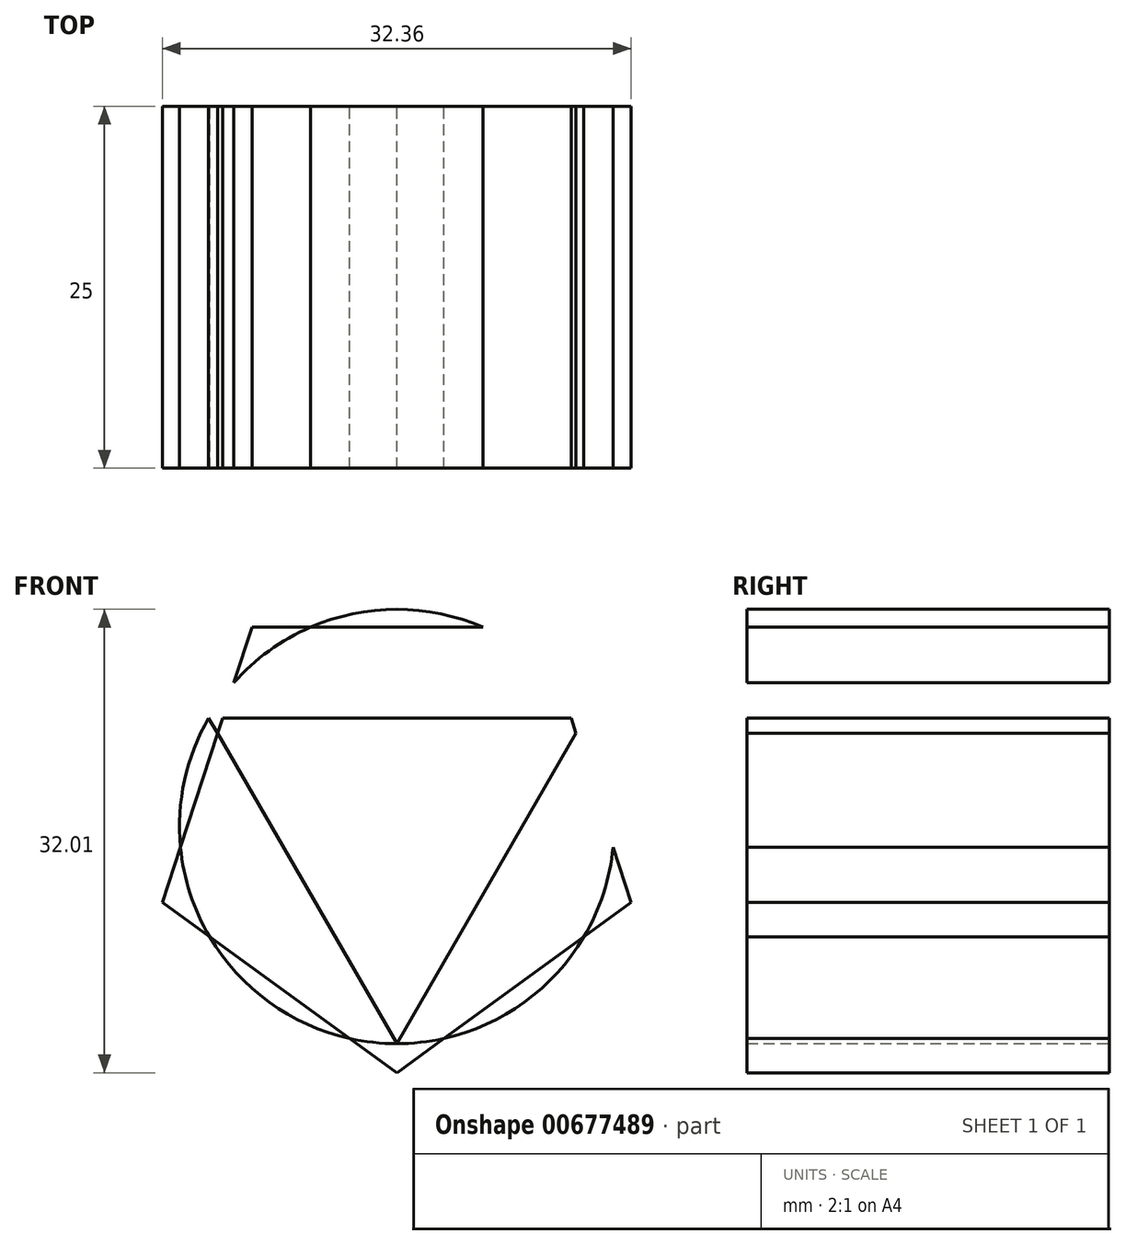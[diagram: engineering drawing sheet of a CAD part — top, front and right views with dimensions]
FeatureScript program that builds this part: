
annotation { "Feature Type Name" : "Feature", "Feature Type Description" : "" }
export const myFeature = defineFeature(function(context is Context, id is Id, definition is map)
    precondition{}
    {
        {
            var Q0;
            Q0=qCreatedBy(makeId("Front.planeOp"),FACE);
            var sketch = newSketch(context, id + "F0", { "sketchPlane" : qUnion([Q0])});
            skCircle(sketch, "E0", {"center": v(0, 0) * mm, "radius": 15 * mm});
            skCircle(sketch, "E1.cCircle", {"center": v(0, 0) * mm, "radius": 13.76 * mm, "construction": true});
            skLineSegment(sketch, "E1.0", {"start": v(10, 13.76) * mm, "end": v(-10, 13.76) * mm});
            skLineSegment(sketch, "E1.1", {"start": v(16.18, -5.26) * mm, "end": v(10, 13.76) * mm});
            skLineSegment(sketch, "E1.2", {"start": v(0, -17.01) * mm, "end": v(16.18, -5.26) * mm});
            skLineSegment(sketch, "E1.3", {"start": v(-16.18, -5.26) * mm, "end": v(0, -17.01) * mm});
            skLineSegment(sketch, "E1.4", {"start": v(-10, 13.76) * mm, "end": v(-16.18, -5.26) * mm});
            skPoint(sketch, "E1.0.midPoint", {"position": v(0, 13.76) * mm});
            skCircle(sketch, "E2.cCircle", {"center": v(0, 0) * mm, "radius": 7.5 * mm, "construction": true});
            skLineSegment(sketch, "E2.0", {"start": v(-13, 7.5) * mm, "end": v(13, 7.5) * mm});
            skLineSegment(sketch, "E2.1", {"start": v(13, 7.5) * mm, "end": v(0, -15) * mm});
            skLineSegment(sketch, "E2.2", {"start": v(0, -15) * mm, "end": v(-13, 7.5) * mm});
            skPoint(sketch, "E2.0.midPoint", {"position": v(0, 7.5) * mm});
            skSolve(sketch);
        }
        {
            var Q0;
            Q0=sQuery(id+"F0.wireOp",EDGE,"E1.2");
            var Q1;
            Q1=sQuery(id+"F0.wireOp",EDGE,"E1.1");
            var Q2;
            Q2=sQuery(id+"F0.wireOp",EDGE,"E1.0");
            var Q3;
            Q3=sQuery(id+"F0.wireOp",EDGE,"E1.4");
            var Q4;
            Q4=sQuery(id+"F0.wireOp",EDGE,"E1.3");
            extrude(context, id + "F1", {"bodyType" : ToolBodyType.SURFACE, "surfaceEntities" : qUnion([Q0, Q1, Q2, Q3, Q4]), "depth" : 25 * mm, "offsetDistance" : 25 * mm});
        }
        {
            var Q0;
            Q0=sQuery(id+"F0.wireOp",EDGE,"E0");
            extrude(context, id + "F2", {"bodyType" : ToolBodyType.SURFACE, "surfaceEntities" : qUnion([Q0]), "depth" : 25 * mm, "offsetDistance" : 25 * mm});
        }
        {
            var Q0;
            {var subQ1=sQuery(id+"F0.wireOp",EDGE,"E2.1");var subQ3=sQuery(id+"F0.wireOp",EDGE,"E1.1");var subQ4=makeQuery(id+"F0.imprint","INTERSECT",VERTEX,{"derivedFrom":[subQ3,subQ1]});Q0=makeQuery(id+"F0.imprint","IMPRINT",FACE,{"disambiguationData":[TD([[makeQuery(id+"F0.imprint","IMPRINT",EDGE,{"disambiguationData":[TD([[subQ4,-1.0]])],"derivedFrom":subQ3}),1.0]])]});}
            var Q1;
            Q1=sQuery(id+"F0.wireOp",EDGE,"E2.2");
            var Q2;
            Q2=sQuery(id+"F0.wireOp",EDGE,"E2.0");
            var Q3;
            Q3=sQuery(id+"F0.wireOp",EDGE,"E2.1");
            extrude(context, id + "F3", {"entities" : qUnion([Q0]), "surfaceEntities" : qUnion([Q1, Q2, Q3]), "depth" : 25 * mm, "offsetDistance" : 25 * mm});
        }
        {
            var Q0;
            {var subQ0=sQuery(id+"F0.wireOp",EDGE,"E1.0");var subQ1=sQuery(id+"F0.wireOp",EDGE,"E0");var subQ2=makeQuery(id+"F0.imprint","INTERSECT",VERTEX,{"disambiguationData":[OD(1.0)],"derivedFrom":[subQ1,subQ0]});Q0=makeQuery(id+"F0.imprint","IMPRINT",FACE,{"disambiguationData":[TD([[makeQuery(id+"F0.imprint","IMPRINT",EDGE,{"disambiguationData":[TD([[subQ2,-1.0]])],"derivedFrom":subQ1}),-1.0]])]});}
            var Q1;
            {var subQ0=sQuery(id+"F0.wireOp",EDGE,"E1.4");var subQ1=sQuery(id+"F0.wireOp",EDGE,"E0");var subQ2=makeQuery(id+"F0.imprint","INTERSECT",VERTEX,{"disambiguationData":[OD(1.0)],"derivedFrom":[subQ1,subQ0]});Q1=makeQuery(id+"F0.imprint","IMPRINT",FACE,{"disambiguationData":[TD([[makeQuery(id+"F0.imprint","IMPRINT",EDGE,{"disambiguationData":[TD([[subQ2,-1.0]])],"derivedFrom":subQ1}),-1.0]])]});}
            var Q2;
            {var subQ2=sQuery(id+"F0.wireOp",EDGE,"E1.3");var subQ4=sQuery(id+"F0.wireOp",EDGE,"E1.2");var subQ6=makeQuery(id+"F0.imprint","INTERSECT",VERTEX,{"derivedFrom":[subQ4,subQ2]});Q2=makeQuery(id+"F0.imprint","IMPRINT",FACE,{"disambiguationData":[TD([[makeQuery(id+"F0.imprint","IMPRINT",EDGE,{"disambiguationData":[TD([[subQ6,-1.0]])],"derivedFrom":subQ4}),1.0]])]});}
            var Q3;
            {var subQ0=sQuery(id+"F0.wireOp",EDGE,"E1.2");var subQ1=sQuery(id+"F0.wireOp",EDGE,"E0");var subQ2=makeQuery(id+"F0.imprint","INTERSECT",VERTEX,{"disambiguationData":[OD(1.0)],"derivedFrom":[subQ1,subQ0]});Q3=makeQuery(id+"F0.imprint","IMPRINT",FACE,{"disambiguationData":[TD([[makeQuery(id+"F0.imprint","IMPRINT",EDGE,{"disambiguationData":[TD([[subQ2,-1.0]])],"derivedFrom":subQ1}),-1.0]])]});}
            var Q4;
            {var subQ0=sQuery(id+"F0.wireOp",EDGE,"E1.1");var subQ1=sQuery(id+"F0.wireOp",EDGE,"E0");var subQ2=makeQuery(id+"F0.imprint","INTERSECT",VERTEX,{"disambiguationData":[OD(0.0)],"derivedFrom":[subQ1,subQ0]});Q4=makeQuery(id+"F0.imprint","IMPRINT",FACE,{"disambiguationData":[TD([[makeQuery(id+"F0.imprint","IMPRINT",EDGE,{"disambiguationData":[TD([[subQ2,-1.0]])],"derivedFrom":subQ1}),-1.0]])]});}
            var Q5;
            {var subQ0=sQuery(id+"F0.wireOp",EDGE,"E1.0");var subQ1=sQuery(id+"F0.wireOp",EDGE,"E0");var subQ2=makeQuery(id+"F0.imprint","INTERSECT",VERTEX,{"disambiguationData":[OD(0.0)],"derivedFrom":[subQ1,subQ0]});Q5=makeQuery(id+"F0.imprint","IMPRINT",FACE,{"disambiguationData":[TD([[makeQuery(id+"F0.imprint","IMPRINT",EDGE,{"disambiguationData":[TD([[subQ2,-1.0]])],"derivedFrom":subQ1}),1.0]])]});}
            var Q6;
            {var subQ1=sQuery(id+"F0.wireOp",EDGE,"E0");var subQ3=sQuery(id+"F0.wireOp",EDGE,"E1.1");var subQ4=makeQuery(id+"F0.imprint","INTERSECT",VERTEX,{"disambiguationData":[OD(1.0)],"derivedFrom":[subQ1,subQ3]});Q6=makeQuery(id+"F0.imprint","IMPRINT",FACE,{"disambiguationData":[TD([[makeQuery(id+"F0.imprint","IMPRINT",EDGE,{"disambiguationData":[TD([[subQ4,-1.0]])],"derivedFrom":subQ3}),-1.0]])]});}
            var Q7;
            {var subQ0=sQuery(id+"F0.wireOp",EDGE,"E1.2");var subQ1=sQuery(id+"F0.wireOp",EDGE,"E0");var subQ2=makeQuery(id+"F0.imprint","INTERSECT",VERTEX,{"disambiguationData":[OD(0.0)],"derivedFrom":[subQ1,subQ0]});Q7=makeQuery(id+"F0.imprint","IMPRINT",FACE,{"disambiguationData":[TD([[makeQuery(id+"F0.imprint","IMPRINT",EDGE,{"disambiguationData":[TD([[subQ2,-1.0]])],"derivedFrom":subQ1}),1.0]])]});}
            var Q8;
            {var subQ0=sQuery(id+"F0.wireOp",EDGE,"E1.3");var subQ1=sQuery(id+"F0.wireOp",EDGE,"E0");var subQ2=makeQuery(id+"F0.imprint","INTERSECT",VERTEX,{"disambiguationData":[OD(0.0)],"derivedFrom":[subQ1,subQ0]});Q8=makeQuery(id+"F0.imprint","IMPRINT",FACE,{"disambiguationData":[TD([[makeQuery(id+"F0.imprint","IMPRINT",EDGE,{"disambiguationData":[TD([[subQ2,-1.0]])],"derivedFrom":subQ1}),1.0]])]});}
            var Q9;
            {var subQ1=sQuery(id+"F0.wireOp",EDGE,"E0");var subQ3=sQuery(id+"F0.wireOp",EDGE,"E1.4");var subQ4=makeQuery(id+"F0.imprint","INTERSECT",VERTEX,{"disambiguationData":[OD(1.0)],"derivedFrom":[subQ1,subQ3]});Q9=makeQuery(id+"F0.imprint","IMPRINT",FACE,{"disambiguationData":[TD([[makeQuery(id+"F0.imprint","IMPRINT",EDGE,{"disambiguationData":[TD([[subQ4,1.0]])],"derivedFrom":subQ3}),-1.0]])]});}
            extrude(context, id + "F4", {"entities" : qUnion([Q0, Q1, Q2, Q3, Q4, Q5, Q6, Q7, Q8, Q9]), "operationType" : NewBodyOperationType.ADD, "depth" : 25 * mm, "offsetDistance" : 25 * mm});
        }
    });
